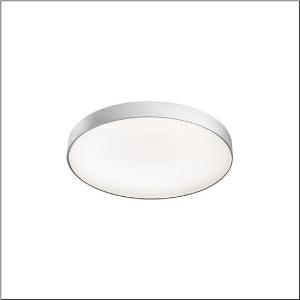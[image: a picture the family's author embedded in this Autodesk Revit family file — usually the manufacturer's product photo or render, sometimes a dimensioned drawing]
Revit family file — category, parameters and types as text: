
# Revit family: round_21_m_51mr36nd0421s
name_source: partatom
category: Lighting Fixtures
units: mm (PartAtom-declared; Revit-internal decimal feet)

## family parameters
Cut with Voids When Loaded = No
Host = Face
Light Source = No
Part Type = Normal
Room Calculation Point = No
Round Connector Dimension = Use Diameter
Shared = No

## types (1)
- Round 21 M (1 x LED, 7470 lm, 54.6 W, 4000K)
    Apparent Load = 55 VA
    CIE Flux Codes = 66 90 98 84 100
    Color Rendering = 80
    Color Temperature = 4000K
    Default Elevation = 1800 mm
    Description = Round 21 M, wall and ceiling luminaire, primary optical cover: micro prismatic cover, of PMMA, transparent, CAT 2 (L<= 3000cd/m²), light emission: direct/indirect distribution, primary light characteristic: symmetric, installation type: surface-mounted, suspended mounting, LED, rated luminous flux: 7.470lm, luminous efficacy: 137lm/W, light colour: 840, colour temperature: 4000K, control gear: DALI 2, with terminal, 5-pole, mains connection: 230V, AC, 50/60Hz, rated input power: 54.6W, housing, of aluminium, coated, silver, diameter: 600mm, height: 62mm, protection rating (complete): IP40, insulation class (complete): insulation class I (protective earthing), certification: CE, impact resistance: IK04, permissible operating ambient temperature: -10..+35°C, packaging unit: 1 piece
    Height = 87 mm
    Lamp = 1 x LED
    Lamp Light Flux = 7470 lm
    Lamp Power = 54.6 W
    Lamp count = 1
    Length = 600 mm
    Luminous efficacy = 137 lm/W
    Manufacturer = Siteco
    ModVariant = No
    Model = 51MR36ND0421S
    Mounting Place = Ceiling
    Mounting Type = Surface mounted
    Number of Poles = 1
    OnlyDefault = Yes
    Power Factor = 1
    Product Name = Round 21 M
    Product group = wall and ceiling luminaire | ceiling mounted
    ProductGroupID = 304
    Protection Class = Protection class I
    Protection Degree = IP 40
    RLX_Detail_Level = 1
    RLX_Emergency_Light_Flux = 0 lm
    RLX_Emergency_Type = 0
    RLX_Emergency_Type_DB = No
    RlxData = <blob elided: 19033 chars, md5=eb270330>
    Socket = socket
    Standby Power = 0 W
    System Light Flux = 7470 lm
    System Power = 55 W
    Type Comments = Product without accessories
    Type Image = l_1258301.jpg
    URL = http://relux.com
    VarID = ---
    Voltage = 0 V
    Weight = 0.00 kg
    Width = 0 mm  [stored 0 ft]

note: [stored X ft] marks values corroborated as IEEE doubles in the binary element streams (Revit-internal decimal feet)

## geometry (parser evidence)
native form markers: Blend x4, Sweep x13
no freeform markers — native parametric forms only
